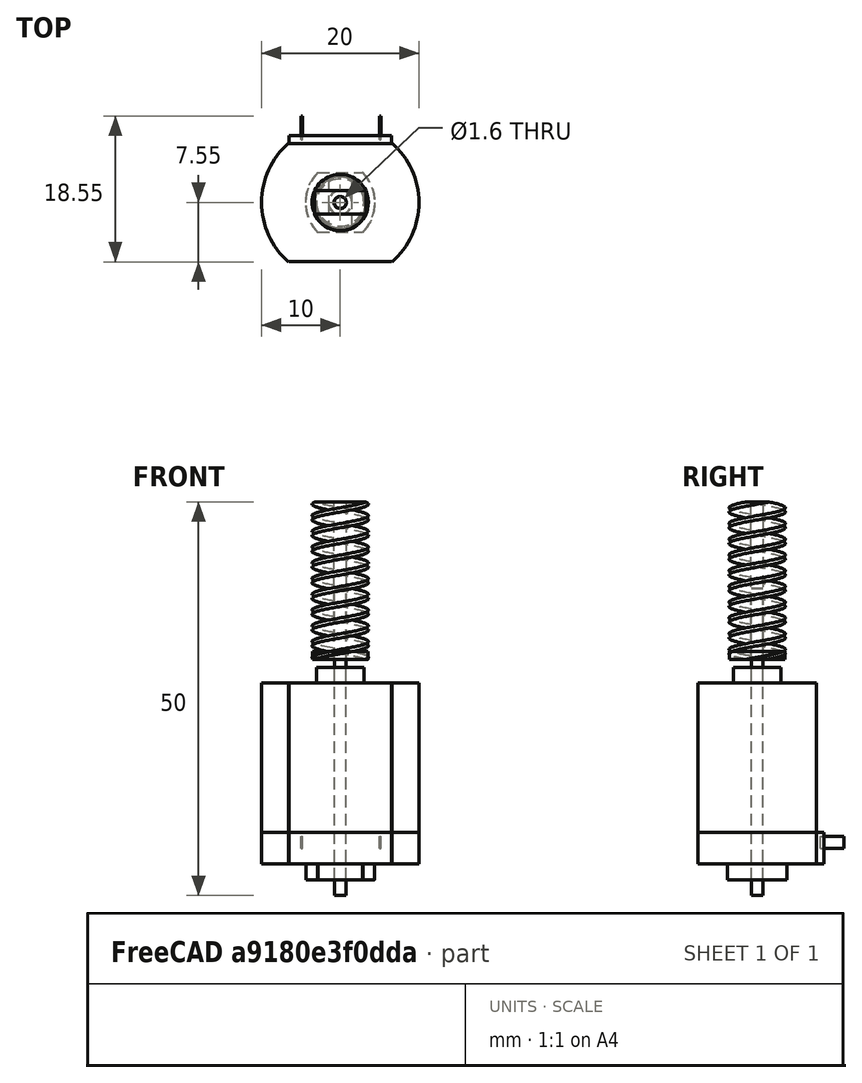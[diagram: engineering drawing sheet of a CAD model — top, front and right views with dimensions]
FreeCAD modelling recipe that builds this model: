
FCSTD DOCUMENT  (FreeCAD 0.15R4671 (Git))
Label: DCMotorMabuchi14withWorm
License: CreativeCommons Attribution-NonCommercial
LicenseURL: http://creativecommons.org/licenses/by-nc/4.0/
objects: Part::Feature×3, Part::Cylinder×2, Part::Box×2, Part::Cut×1
note: 8 computed .brp shape members not serialized (recipe doc carries the construction recipe); baked Part::Feature solids carry a one-line shape summary decoded from their .brp

FEATURE [Part::Feature] Fusion_solid002  label="MotorBodyMetal"
  shape: bbox 20 x 15.09 x 21 mm, 16 faces (baked)
FEATURE [Part::Cylinder] Cylinder  label="MotorAxisShaft"
  Angle = 360
  Height = 39
  Radius = 0.75
FEATURE [Part::Feature] Fusion001  label="MotorBodyPlastic"
  shape: bbox 20 x 16.05 x 6 mm, 27 faces (baked)
FEATURE [Part::Box] Box  label="MotorPinA"
  Height = 1.5
  Length = 0.2
  Placement = pos=(5,8,6) rot=(0,0,1;0rad)
  Width = 3
FEATURE [Part::Box] Box001  label="MotorPinB"
  Height = 1.5
  Length = 0.2
  Placement = pos=(-5,8,6) rot=(0,0,1;0rad)
  Width = 3
FEATURE [Part::Feature] Fusion_solid  label="Fusion (Solid)001"
  shape: bbox 10.12 x 11.2 x 20 mm, 30 faces (baked)
FEATURE [Part::Cylinder] Cylinder001  label="AxisHole"
  Angle = 360
  Height = 23
  Placement = pos=(0,0,-1) rot=(0,0,1;0rad)
  Radius = 0.8
FEATURE [Part::Cut] Cut  label="WormPlastic"
  Base = -> Fusion_solid
  Placement = pos=(0,0,30) rot=(0,0,1;0rad)
  Tool = -> Cylinder001
